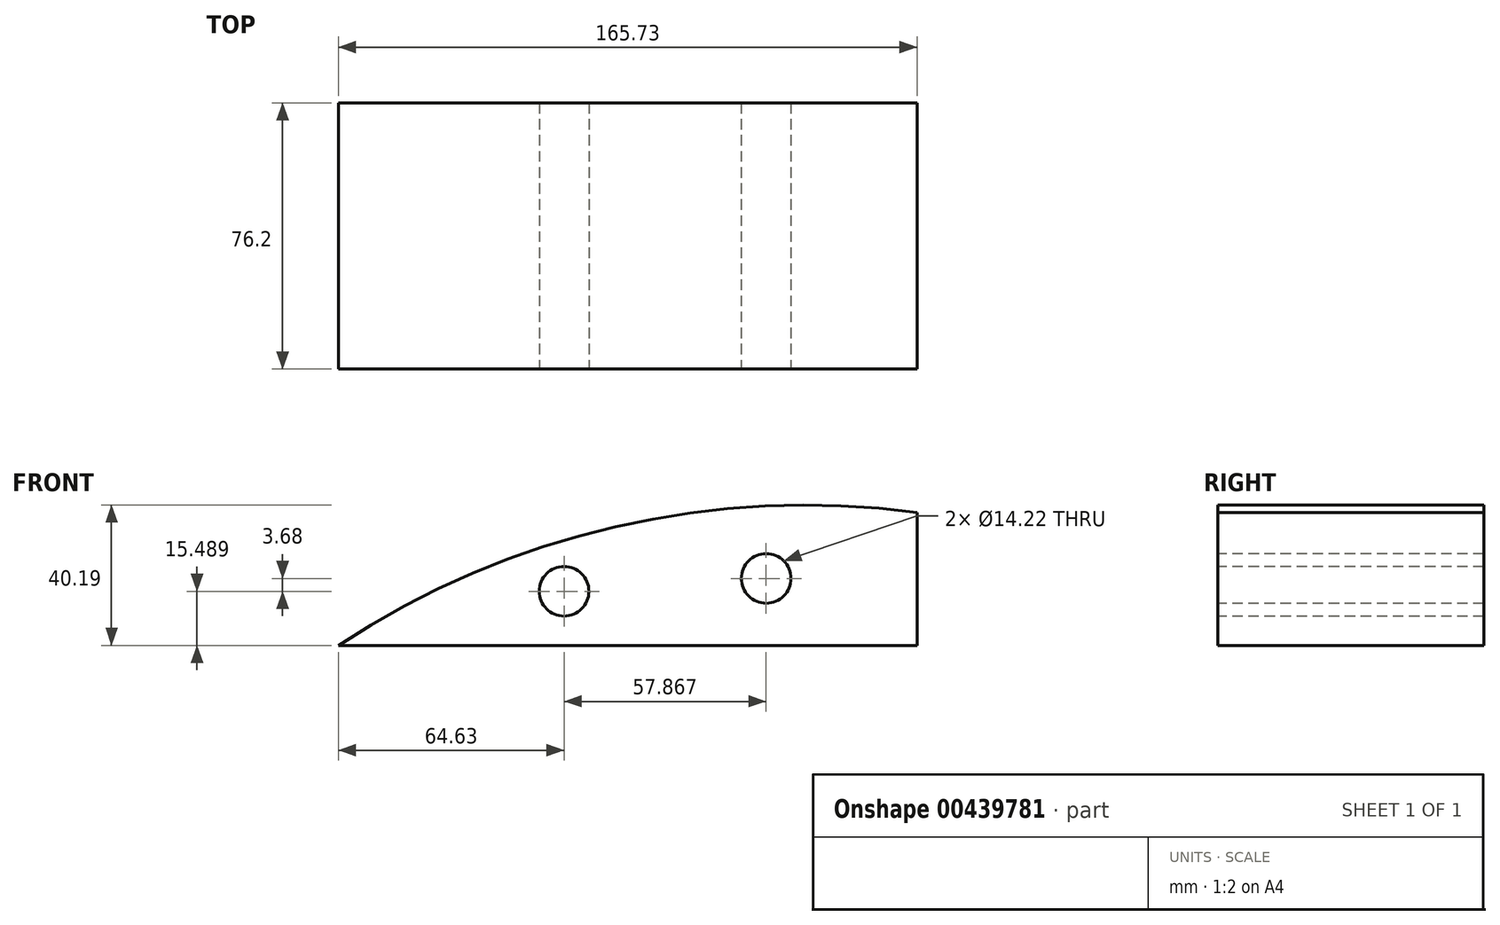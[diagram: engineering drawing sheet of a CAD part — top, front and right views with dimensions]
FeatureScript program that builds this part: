
annotation { "Feature Type Name" : "Feature", "Feature Type Description" : "" }
export const myFeature = defineFeature(function(context is Context, id is Id, definition is map)
    precondition{}
    {
        {
            var Q0;
            Q0=qCreatedBy(makeId("Front.planeOp"),FACE);
            var sketch = newSketch(context, id + "F0", { "sketchPlane" : qUnion([Q0])});
            skLineSegment(sketch, "E0", {"start": v(-87.53, 3.13) * mm, "end": v(78.2, 3.13) * mm});
            skLineSegment(sketch, "E1", {"start": v(78.2, 3.13) * mm, "end": v(78.2, 41.23) * mm});
            skArc(sketch, "E2", {"start": v(78.2, 41.23) * mm, "mid": v(-8.1, 37.14) * mm, "end": v(-87.53, 3.13) * mm});
            skSolve(sketch);
        }
        {
            var Q0;
            Q0 = qSketchRegion(id + "F0", true);
            extrude(context, id + "F1", {"entities" : qUnion([Q0]), "depth" : 76.2 * mm});
        }
        {
            var Q0;
            Q0=makeQuery(id+"F1.opExtrude","CAP_FACE",FACE,{"disambiguationData":[OSD([sQuery(id+"F0.wireOp",EDGE,"E0"),sQuery(id+"F0.wireOp",EDGE,"E1"),sQuery(id+"F0.wireOp",EDGE,"E2")])],"isStart":false});
            var sketch = newSketch(context, id + "F2", { "sketchPlane" : qUnion([Q0])});
            skCircle(sketch, "E3", {"center": v(34.97, 22.3) * mm, "radius": 7.11 * mm});
            skCircle(sketch, "E4", {"center": v(-22.9, 18.62) * mm, "radius": 7.11 * mm});
            skSolve(sketch);
        }
        {
            var Q0;
            Q0=sQuery(id+"F2.wireOp",VERTEX,"E4.center");
            var Q1;
            Q1=sQuery(id+"F2.wireOp",VERTEX,"E3.center");
            var Q2;
            Q2=makeQuery(id+"F1.opExtrude","SWEPT_BODY",BODY,{"disambiguationData":[OSD([sQuery(id+"F0.wireOp",EDGE,"E0"),sQuery(id+"F0.wireOp",EDGE,"E1"),sQuery(id+"F0.wireOp",EDGE,"E2")])]});
            hole(context, id + "F3", {"style" : HoleStyle.SIMPLE, "endStyle" : HoleEndStyle.THROUGH, "holeDiameter" : 14.22 * mm, "isTappedThrough" : true, "tappedDepth" : 12.7 * mm, "tapClearance" : 3, "startFromSketch" : true, "locations" : qUnion([Q0, Q1]), "scope" : qUnion([Q2])});
        }
    });
